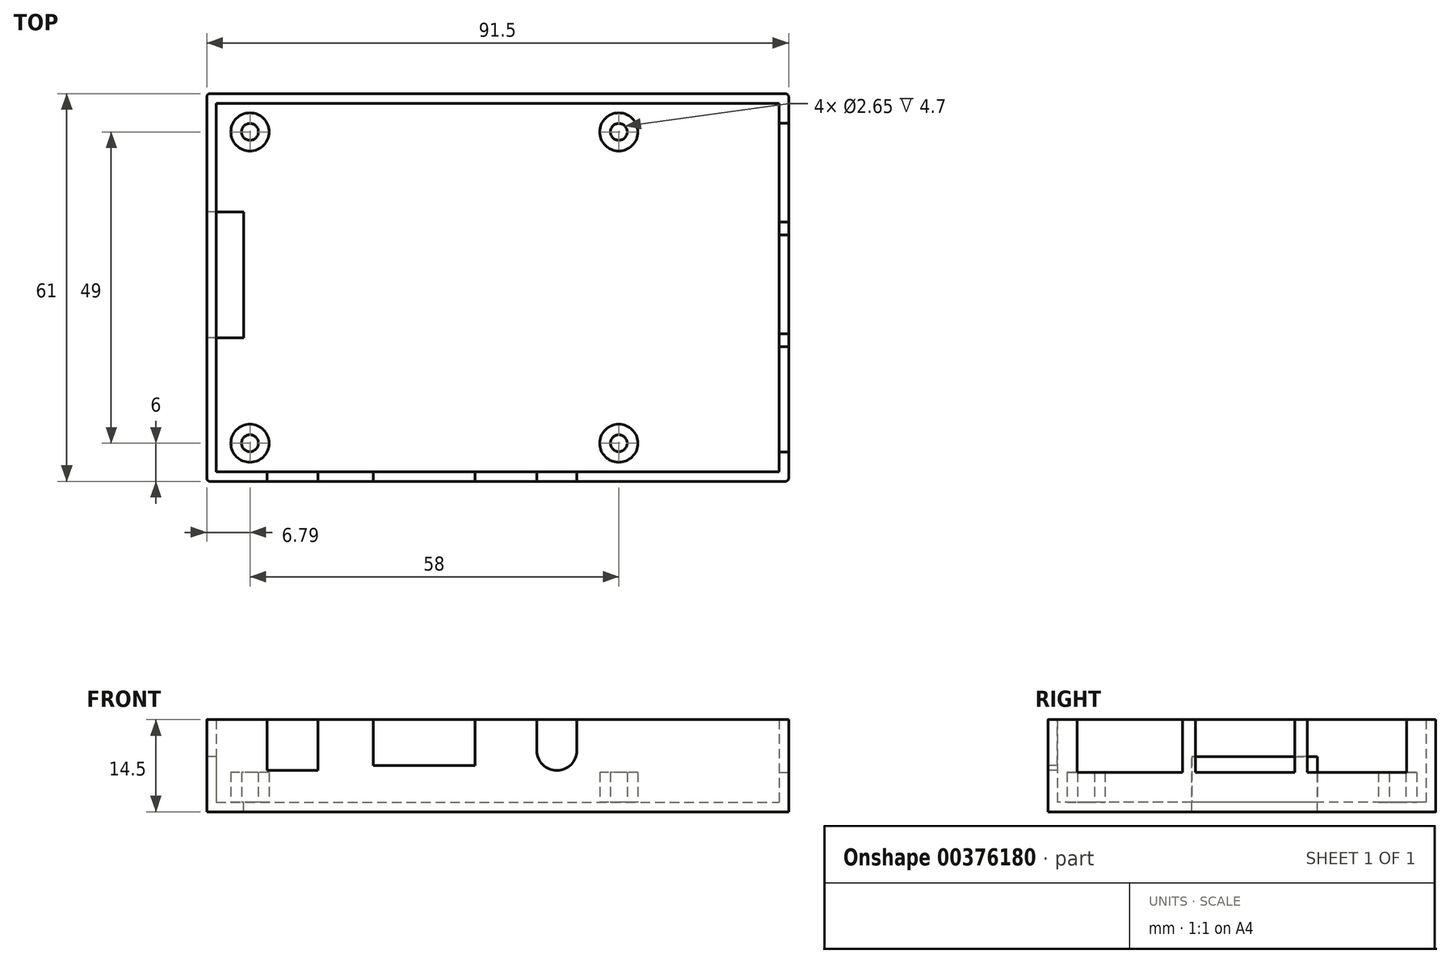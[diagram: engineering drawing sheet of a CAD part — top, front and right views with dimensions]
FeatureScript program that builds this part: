
annotation { "Feature Type Name" : "Feature", "Feature Type Description" : "" }
export const myFeature = defineFeature(function(context is Context, id is Id, definition is map)
    precondition{}
    {
        {
            var Q0;
            Q0=qCreatedBy(makeId("Top.planeOp"),FACE);
            var sketch = newSketch(context, id + "F0", { "sketchPlane" : qUnion([Q0])});
            skLineSegment(sketch, "E0.bottom", {"start": v(-45.75, 30.5) * mm, "end": v(45.75, 30.5) * mm});
            skLineSegment(sketch, "E0.top", {"start": v(-45.75, -30.5) * mm, "end": v(45.75, -30.5) * mm});
            skLineSegment(sketch, "E0.left", {"start": v(-45.75, 30.5) * mm, "end": v(-45.75, -30.5) * mm});
            skLineSegment(sketch, "E0.right", {"start": v(45.75, 30.5) * mm, "end": v(45.75, -30.5) * mm});
            skPoint(sketch, "E0.middle", {"position": v(0, 0) * mm});
            skSolve(sketch);
        }
        {
            var Q0;
            Q0=makeQuery(id+"F0.imprint","IMPRINT",FACE,{"disambiguationData":[TD([[makeQuery(id+"F0.imprint","IMPRINT",EDGE,{"derivedFrom":sQuery(id+"F0.wireOp",EDGE,"E0.bottom")}),-1.0]])]});
            extrude(context, id + "F1", {"entities" : qUnion([Q0]), "depth" : 14.5 * mm});
        }
        {
            var Q0;
            Q0=makeQuery(id+"F1.opExtrude","CAP_FACE",FACE,{"disambiguationData":[OSD([sQuery(id+"F0.wireOp",EDGE,"E0.bottom"),sQuery(id+"F0.wireOp",EDGE,"E0.top"),sQuery(id+"F0.wireOp",EDGE,"E0.left"),sQuery(id+"F0.wireOp",EDGE,"E0.right")])],"isStart":false});
            shell(context, id + "F2", {"entities" : qUnion([Q0]), "thickness" : 1.5 * mm});
        }
        {
            var Q0;
            Q0=makeQuery(id+"F1.opExtrude","SWEPT_FACE",FACE,{"disambiguationData":[OSD([sQuery(id+"F0.wireOp",EDGE,"E0.top")])]});
            var sketch = newSketch(context, id + "F3", { "sketchPlane" : qUnion([Q0])});
            skLineSegment(sketch, "E1.bottom", {"start": v(-28.25, 6.5) * mm, "end": v(-36.25, 6.5) * mm});
            skLineSegment(sketch, "E1.top", {"start": v(-28.25, 14.5) * mm, "end": v(-36.25, 14.5) * mm});
            skLineSegment(sketch, "E1.left", {"start": v(-28.25, 6.5) * mm, "end": v(-28.25, 14.5) * mm});
            skLineSegment(sketch, "E1.right", {"start": v(-36.25, 6.5) * mm, "end": v(-36.25, 14.5) * mm});
            skPoint(sketch, "E1.middle", {"position": v(-32.25, 10.5) * mm});
            skLineSegment(sketch, "E2.bottom", {"start": v(-3.55, 14.5) * mm, "end": v(-19.55, 14.5) * mm});
            skLineSegment(sketch, "E2.top", {"start": v(-3.55, 7.3) * mm, "end": v(-19.55, 7.3) * mm});
            skLineSegment(sketch, "E2.left", {"start": v(-3.55, 14.5) * mm, "end": v(-3.55, 7.3) * mm});
            skLineSegment(sketch, "E2.right", {"start": v(-19.55, 14.5) * mm, "end": v(-19.55, 7.3) * mm});
            skPoint(sketch, "E2.middle", {"position": v(-11.55, 10.9) * mm});
            skCircle(sketch, "E3", {"center": v(9.3, 9.65) * mm, "radius": 3.15 * mm});
            skLineSegment(sketch, "E4.top", {"start": v(12.45, 14.5) * mm, "end": v(6.15, 14.5) * mm});
            skLineSegment(sketch, "E4.left", {"start": v(12.45, 9.65) * mm, "end": v(12.45, 14.5) * mm});
            skLineSegment(sketch, "E4.right", {"start": v(6.15, 9.65) * mm, "end": v(6.15, 14.5) * mm});
            skSolve(sketch);
        }
        {
            var Q0;
            Q0 = qSketchRegion(id + "F3", true);
            extrude(context, id + "F4", {"entities" : qUnion([Q0]), "operationType" : NewBodyOperationType.REMOVE, "oppositeDirection" : true, "depth" : 2.1 * mm});
        }
        {
            var Q0;
            Q0=makeQuery(id+"F1.opExtrude","SWEPT_FACE",FACE,{"disambiguationData":[OSD([sQuery(id+"F0.wireOp",EDGE,"E0.left")])]});
            var sketch = newSketch(context, id + "F5", { "sketchPlane" : qUnion([Q0])});
            skLineSegment(sketch, "E5.bottom", {"start": v(7.9, 0) * mm, "end": v(-11.9, 0) * mm});
            skLineSegment(sketch, "E5.top", {"start": v(7.9, 8.7) * mm, "end": v(-11.9, 8.7) * mm});
            skLineSegment(sketch, "E5.left", {"start": v(7.9, 0) * mm, "end": v(7.9, 8.7) * mm});
            skLineSegment(sketch, "E5.right", {"start": v(-11.9, 0) * mm, "end": v(-11.9, 8.7) * mm});
            skSolve(sketch);
        }
        {
            var Q0;
            Q0 = qSketchRegion(id + "F5", true);
            extrude(context, id + "F6", {"entities" : qUnion([Q0]), "operationType" : NewBodyOperationType.REMOVE, "oppositeDirection" : true, "depth" : 5.8 * mm});
        }
        {
            var Q0;
            Q0=makeQuery(id+"F1.opExtrude","SWEPT_FACE",FACE,{"disambiguationData":[OSD([sQuery(id+"F0.wireOp",EDGE,"E0.right")])]});
            var sketch = newSketch(context, id + "F7", { "sketchPlane" : qUnion([Q0])});
            skLineSegment(sketch, "E6.bottom", {"start": v(-25.9, 14.5) * mm, "end": v(-9.3, 14.5) * mm});
            skLineSegment(sketch, "E6.top", {"start": v(-25.9, 6.2) * mm, "end": v(-9.3, 6.2) * mm});
            skLineSegment(sketch, "E6.left", {"start": v(-25.9, 14.5) * mm, "end": v(-25.9, 6.2) * mm});
            skLineSegment(sketch, "E6.right", {"start": v(-9.3, 14.5) * mm, "end": v(-9.3, 6.2) * mm});
            skLineSegment(sketch, "E7.bottom", {"start": v(-7.3, 14.5) * mm, "end": v(8.3, 14.5) * mm});
            skLineSegment(sketch, "E7.top", {"start": v(-7.3, 6.2) * mm, "end": v(8.3, 6.2) * mm});
            skLineSegment(sketch, "E7.left", {"start": v(-7.3, 14.5) * mm, "end": v(-7.3, 6.2) * mm});
            skLineSegment(sketch, "E7.right", {"start": v(8.3, 14.5) * mm, "end": v(8.3, 6.2) * mm});
            skLineSegment(sketch, "E8.bottom", {"start": v(25.9, 6.2) * mm, "end": v(10.3, 6.2) * mm});
            skLineSegment(sketch, "E8.top", {"start": v(25.9, 14.5) * mm, "end": v(10.3, 14.5) * mm});
            skLineSegment(sketch, "E8.left", {"start": v(25.9, 6.2) * mm, "end": v(25.9, 14.5) * mm});
            skLineSegment(sketch, "E8.right", {"start": v(10.3, 6.2) * mm, "end": v(10.3, 14.5) * mm});
            skSolve(sketch);
        }
        {
            var Q0;
            Q0 = qSketchRegion(id + "F7", true);
            extrude(context, id + "F8", {"entities" : qUnion([Q0]), "operationType" : NewBodyOperationType.REMOVE, "oppositeDirection" : true, "depth" : 3 * mm});
        }
        {
            var Q0;
            Q0=makeQuery(id+"F2.opShell","OFFSET_FACE",FACE,{"disambiguationData":[OSD([sQuery(id+"F0.wireOp",EDGE,"E0.bottom"),sQuery(id+"F0.wireOp",EDGE,"E0.top"),sQuery(id+"F0.wireOp",EDGE,"E0.left"),sQuery(id+"F0.wireOp",EDGE,"E0.right")])]});
            var sketch = newSketch(context, id + "F9", { "sketchPlane" : qUnion([Q0])});
            skCircle(sketch, "E9", {"center": v(19.04, 24.5) * mm, "radius": 3 * mm});
            skCircle(sketch, "E10", {"center": v(19.04, 24.5) * mm, "radius": 1.32 * mm});
            skCircle(sketch, "E11", {"center": v(19.04, -24.5) * mm, "radius": 3 * mm});
            skCircle(sketch, "E12", {"center": v(19.04, -24.5) * mm, "radius": 1.32 * mm});
            skCircle(sketch, "E13", {"center": v(-38.96, 24.5) * mm, "radius": 3 * mm});
            skCircle(sketch, "E14", {"center": v(-38.96, 24.5) * mm, "radius": 1.32 * mm});
            skCircle(sketch, "E15", {"center": v(-38.96, -24.5) * mm, "radius": 3 * mm});
            skCircle(sketch, "E16", {"center": v(-38.96, -24.5) * mm, "radius": 1.32 * mm});
            skSolve(sketch);
        }
        {
            var Q0;
            Q0 = qSketchRegion(id + "F9", true);
            extrude(context, id + "F10", {"entities" : qUnion([Q0]), "operationType" : NewBodyOperationType.ADD, "depth" : 4.7 * mm});
        }
        {
            var Q0;
            Q0=makeQuery(id+"F1.opExtrude","SWEPT_EDGE",EDGE,{"disambiguationData":[OSD([sQuery(id+"F0.wireOp",EDGE,"E0.top"),sQuery(id+"F0.wireOp",EDGE,"E0.left")])]});
            var Q1;
            Q1=makeQuery(id+"F1.opExtrude","SWEPT_EDGE",EDGE,{"disambiguationData":[OSD([sQuery(id+"F0.wireOp",EDGE,"E0.bottom"),sQuery(id+"F0.wireOp",EDGE,"E0.left")])]});
            var Q2;
            Q2=makeQuery(id+"F1.opExtrude","SWEPT_EDGE",EDGE,{"disambiguationData":[OSD([sQuery(id+"F0.wireOp",EDGE,"E0.top"),sQuery(id+"F0.wireOp",EDGE,"E0.right")])]});
            var Q3;
            Q3=makeQuery(id+"F1.opExtrude","SWEPT_EDGE",EDGE,{"disambiguationData":[OSD([sQuery(id+"F0.wireOp",EDGE,"E0.bottom"),sQuery(id+"F0.wireOp",EDGE,"E0.right")])]});
            fillet(context, id + "F11", {"entities" : qUnion([Q0, Q1, Q2, Q3]), "radius" : .5 * mm, "tangentPropagation" : true, "allowEdgeOverflow" : false});
        }
    });
